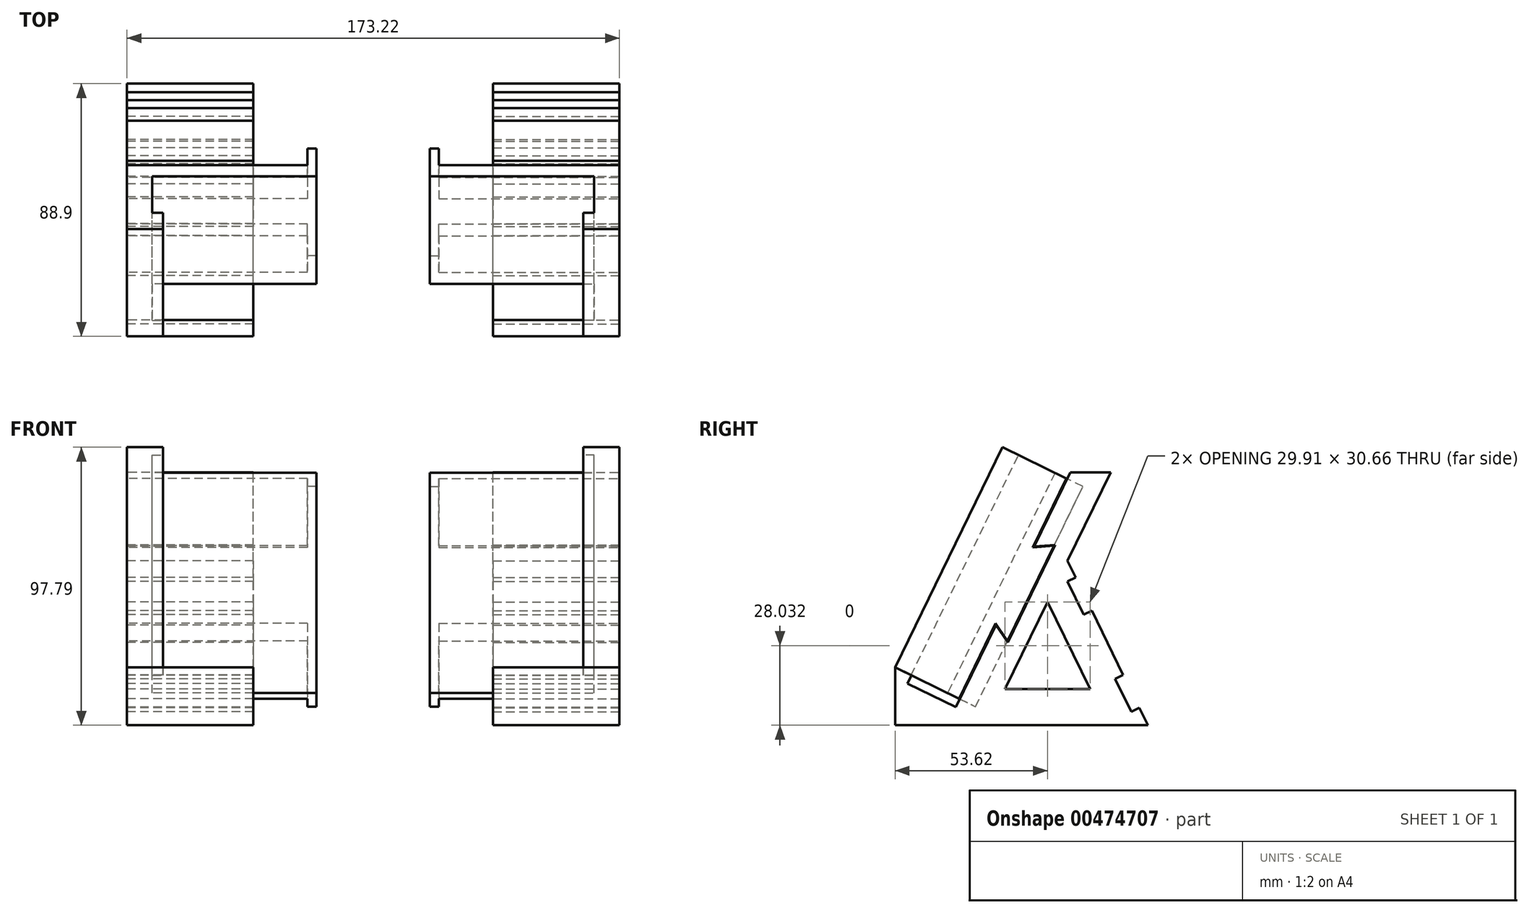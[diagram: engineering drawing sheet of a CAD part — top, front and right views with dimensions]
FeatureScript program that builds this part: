
annotation { "Feature Type Name" : "Feature", "Feature Type Description" : "" }
export const myFeature = defineFeature(function(context is Context, id is Id, definition is map)
    precondition{}
    {
        {
            var Q0;
            Q0=qCreatedBy(makeId("Front.planeOp"),FACE);
            var sketch = newSketch(context, id + "F0", { "sketchPlane" : qUnion([Q0])});
            skLineSegment(sketch, "E0.bottom", {"start": v(42.16, 0) * mm, "end": v(86.61, 0) * mm});
            skLineSegment(sketch, "E0.top", {"start": v(42.16, 88.9) * mm, "end": v(86.61, 88.9) * mm});
            skLineSegment(sketch, "E0.left", {"start": v(42.16, 0) * mm, "end": v(42.16, 88.9) * mm});
            skLineSegment(sketch, "E0.right", {"start": v(86.61, 0) * mm, "end": v(86.61, 88.9) * mm});
            skSolve(sketch);
        }
        {
            var Q0;
            Q0=makeQuery(id+"F0.imprint","IMPRINT",FACE,{"disambiguationData":[TD([[makeQuery(id+"F0.imprint","IMPRINT",EDGE,{"derivedFrom":sQuery(id+"F0.wireOp",EDGE,"E0.bottom")}),1.0]])]});
            extrude(context, id + "F1", {"entities" : qUnion([Q0]), "endBound" : BoundingType.SYMMETRIC, "depth" : 88.9 * mm});
        }
        {
            var Q0;
            Q0=makeQuery(id+"F1.opExtrude","SWEPT_FACE",FACE,{"disambiguationData":[OSD([sQuery(id+"F0.wireOp",EDGE,"E0.right")])]});
            var sketch = newSketch(context, id + "F2", { "sketchPlane" : qUnion([Q0])});
            skLineSegment(sketch, "E1", {"start": v(-44.45, 20.34) * mm, "end": v(-21.62, 9.2) * mm});
            skLineSegment(sketch, "E2", {"start": v(-21.62, 9.2) * mm, "end": v(17.25, 88.9) * mm});
            skLineSegment(sketch, "E3", {"start": v(-38.74, 17.55) * mm, "end": v(-40.13, 14.7) * mm});
            skLineSegment(sketch, "E4", {"start": v(-40.13, 14.7) * mm, "end": v(-23.01, 6.35) * mm});
            skLineSegment(sketch, "E5", {"start": v(-23.01, 6.35) * mm, "end": v(-21.62, 9.2) * mm});
            skLineSegment(sketch, "E6", {"start": v(17.25, 88.9) * mm, "end": v(-44.45, 88.9) * mm});
            skLineSegment(sketch, "E7", {"start": v(-44.45, 88.9) * mm, "end": v(-44.45, 20.34) * mm});
            skLineSegment(sketch, "E8", {"start": v(-8.93, 35.22) * mm, "end": v(-4.83, 29.15) * mm});
            skLineSegment(sketch, "E9", {"start": v(-4.83, 29.15) * mm, "end": v(11.87, 63.4) * mm});
            skLineSegment(sketch, "E10", {"start": v(11.87, 63.4) * mm, "end": v(4.56, 62.88) * mm});
            skLineSegment(sketch, "E11", {"start": v(-2.19, 49.05) * mm, "end": v(-44.45, 69.67) * mm});
            skLineSegment(sketch, "E12", {"start": v(-2.19, 49.05) * mm, "end": v(3.52, 46.27) * mm});
            skLineSegment(sketch, "E13", {"start": v(-5.79, 12.7) * mm, "end": v(24.13, 12.7) * mm});
            skLineSegment(sketch, "E14", {"start": v(24.13, 12.7) * mm, "end": v(9.17, 43.36) * mm});
            skLineSegment(sketch, "E15", {"start": v(9.17, 43.36) * mm, "end": v(-5.79, 12.7) * mm});
            skLineSegment(sketch, "E16", {"start": v(16.24, 57.85) * mm, "end": v(31.38, 88.9) * mm});
            skLineSegment(sketch, "E17", {"start": v(31.38, 88.9) * mm, "end": v(44.45, 88.9) * mm});
            skLineSegment(sketch, "E18", {"start": v(16.24, 57.85) * mm, "end": v(44.45, 0) * mm});
            skLineSegment(sketch, "E19", {"start": v(44.45, 0) * mm, "end": v(44.45, 88.9) * mm});
            skLineSegment(sketch, "E20", {"start": v(19.1, 51.98) * mm, "end": v(16.24, 50.6) * mm});
            skLineSegment(sketch, "E21", {"start": v(16.24, 50.6) * mm, "end": v(21.92, 38.95) * mm});
            skLineSegment(sketch, "E22", {"start": v(21.92, 38.95) * mm, "end": v(24.78, 40.34) * mm});
            skLineSegment(sketch, "E23", {"start": v(30.34, 28.92) * mm, "end": v(44.45, 35.8) * mm});
            skLineSegment(sketch, "E24.1.0.0", {"start": v(35.8, 17.74) * mm, "end": v(32.94, 16.35) * mm});
            skLineSegment(sketch, "E24.1.0.1", {"start": v(32.94, 16.35) * mm, "end": v(38.62, 4.7) * mm});
            skLineSegment(sketch, "E24.1.0.2", {"start": v(38.62, 4.7) * mm, "end": v(41.48, 6.1) * mm});
            skLineSegment(sketch, "E24.direction1", {"start": v(16.24, 50.6) * mm, "end": v(32.94, 16.35) * mm, "construction": true});
            skSolve(sketch);
        }
        {
            var Q0;
            Q0 = qSketchRegion(id + "F2", true);
            extrude(context, id + "F3", {"entities" : qUnion([Q0]), "operationType" : NewBodyOperationType.REMOVE, "endBound" : BoundingType.UP_TO_NEXT, "oppositeDirection" : true, "depth" : 25.4 * mm});
        }
        {
            var Q0;
            Q0=makeQuery(id+"F1.opExtrude","SWEPT_FACE",FACE,{"disambiguationData":[OSD([sQuery(id+"F0.wireOp",EDGE,"E0.right")])]});
            var sketch = newSketch(context, id + "F4", { "sketchPlane" : qUnion([Q0])});
            skLineSegment(sketch, "E25.0", {"start": v(11.45, 63.1) * mm, "end": v(4, 62.58) * mm});
            skLineSegment(sketch, "E25.1", {"start": v(-4.86, 29.65) * mm, "end": v(11.45, 63.1) * mm});
            skLineSegment(sketch, "E25.2", {"start": v(-9.05, 35.85) * mm, "end": v(-4.86, 29.65) * mm});
            skLineSegment(sketch, "E26", {"start": v(15.81, 86.82) * mm, "end": v(-21.96, 9.37) * mm});
            skLineSegment(sketch, "E27", {"start": v(15.81, 86.82) * mm, "end": v(-6.68, 97.79) * mm});
            skLineSegment(sketch, "E28", {"start": v(-6.68, 97.79) * mm, "end": v(-44.45, 20.34) * mm});
            skLineSegment(sketch, "E29", {"start": v(-44.45, 20.34) * mm, "end": v(-21.96, 9.37) * mm});
            skSolve(sketch);
        }
        {
            var Q0;
            Q0 = qSketchRegion(id + "F4", true);
            extrude(context, id + "F5", {"entities" : qUnion([Q0]), "oppositeDirection" : true, "depth" : 12.7 * mm});
        }
        {
            var Q0;
            Q0=makeQuery(id+"F5.opExtrude","CAP_FACE",FACE,{"disambiguationData":[OSD([sQuery(id+"F4.wireOp",EDGE,"E25.0"),sQuery(id+"F4.wireOp",EDGE,"E25.1"),sQuery(id+"F4.wireOp",EDGE,"E25.2"),sQuery(id+"F4.wireOp",EDGE,"E26"),sQuery(id+"F4.wireOp",EDGE,"E27"),sQuery(id+"F4.wireOp",EDGE,"E28"),sQuery(id+"F4.wireOp",EDGE,"E29")])],"isStart":false});
            var sketch = newSketch(context, id + "F6", { "sketchPlane" : qUnion([Q0])});
            skLineSegment(sketch, "E30.0", {"start": v(-15.81, 86.82) * mm, "end": v(-4, 62.58) * mm});
            skLineSegment(sketch, "E30.1", {"start": v(-11.45, 63.1) * mm, "end": v(-4, 62.58) * mm});
            skLineSegment(sketch, "E30.2", {"start": v(4.86, 29.65) * mm, "end": v(-11.45, 63.1) * mm});
            skLineSegment(sketch, "E30.3", {"start": v(9.05, 35.85) * mm, "end": v(4.86, 29.65) * mm});
            skLineSegment(sketch, "E30.4", {"start": v(9.05, 35.85) * mm, "end": v(21.96, 9.37) * mm});
            skLineSegment(sketch, "E31", {"start": v(-15.81, 86.82) * mm, "end": v(-11.82, 88.77) * mm});
            skLineSegment(sketch, "E32", {"start": v(-11.82, 88.77) * mm, "end": v(25.96, 11.32) * mm});
            skLineSegment(sketch, "E33", {"start": v(25.96, 11.32) * mm, "end": v(21.96, 9.37) * mm});
            skSolve(sketch);
        }
        {
            var Q0;
            Q0 = qSketchRegion(id + "F6", true);
            extrude(context, id + "F7", {"entities" : qUnion([Q0]), "operationType" : NewBodyOperationType.ADD, "depth" : 50.8 * mm});
        }
        {
            var Q0;
            Q0=makeQuery(id+"F7.opExtrude","CAP_FACE",FACE,{"disambiguationData":[OSD([sQuery(id+"F6.wireOp",EDGE,"E30.0"),sQuery(id+"F6.wireOp",EDGE,"E30.1"),sQuery(id+"F6.wireOp",EDGE,"E30.2"),sQuery(id+"F6.wireOp",EDGE,"E30.3"),sQuery(id+"F6.wireOp",EDGE,"E30.4"),sQuery(id+"F6.wireOp",EDGE,"E31"),sQuery(id+"F6.wireOp",EDGE,"E32"),sQuery(id+"F6.wireOp",EDGE,"E33")])],"isStart":false});
            var sketch = newSketch(context, id + "F8", { "sketchPlane" : qUnion([Q0])});
            skLineSegment(sketch, "E34", {"start": v(-11.82, 88.77) * mm, "end": v(25.96, 11.32) * mm});
            skLineSegment(sketch, "E35", {"start": v(25.96, 11.32) * mm, "end": v(16.14, 6.53) * mm});
            skLineSegment(sketch, "E36", {"start": v(16.14, 6.53) * mm, "end": v(-21.63, 83.98) * mm});
            skLineSegment(sketch, "E37", {"start": v(-21.63, 83.98) * mm, "end": v(-11.82, 88.77) * mm});
            skSolve(sketch);
        }
        {
            var Q0;
            Q0 = qSketchRegion(id + "F8", true);
            extrude(context, id + "F9", {"entities" : qUnion([Q0]), "operationType" : NewBodyOperationType.ADD, "depth" : 3.17 * mm});
        }
        {
            var Q0;
            Q0=makeQuery(id+"F9.boolean.opBoolean","MERGE",FACE,{"derivedFrom":[makeQuery(id+"F7.boolean.opBoolean","MERGE",FACE,{"derivedFrom":[makeQuery(id+"F5.opExtrude","SWEPT_FACE",FACE,{"disambiguationData":[OSD([sQuery(id+"F4.wireOp",EDGE,"E27")])]}),makeQuery(id+"F7.opExtrude","SWEPT_FACE",FACE,{"disambiguationData":[OSD([sQuery(id+"F6.wireOp",EDGE,"E31")])]})]}),makeQuery(id+"F9.opExtrude","SWEPT_FACE",FACE,{"disambiguationData":[OSD([sQuery(id+"F8.wireOp",EDGE,"E37")])]})]});
            var sketch = newSketch(context, id + "F10", { "sketchPlane" : qUnion([Q0])});
            skLineSegment(sketch, "E38", {"start": v(73.91, -28.3) * mm, "end": v(77.72, -28.3) * mm});
            skLineSegment(sketch, "E39", {"start": v(77.72, -28.3) * mm, "end": v(77.72, -42.58) * mm});
            skLineSegment(sketch, "E40", {"start": v(73.91, -42.58) * mm, "end": v(73.91, -28.3) * mm});
            skLineSegment(sketch, "E41", {"start": v(77.72, -42.58) * mm, "end": v(73.91, -42.58) * mm});
            skSolve(sketch);
        }
        {
            var Q0;
            Q0 = qSketchRegion(id + "F10", true);
            extrude(context, id + "F11", {"entities" : qUnion([Q0]), "operationType" : NewBodyOperationType.REMOVE, "endBound" : BoundingType.UP_TO_NEXT, "oppositeDirection" : true, "depth" : 25.4 * mm});
        }
        {
            var Q0;
            Q0=makeQuery(id+"F1.opExtrude","SWEPT_BODY",BODY,{"disambiguationData":[OSD([sQuery(id+"F0.wireOp",EDGE,"E0.bottom"),sQuery(id+"F0.wireOp",EDGE,"E0.top"),sQuery(id+"F0.wireOp",EDGE,"E0.left"),sQuery(id+"F0.wireOp",EDGE,"E0.right")])]});
            var Q1;
            Q1=makeQuery(id+"F5.opExtrude","SWEPT_BODY",BODY,{"disambiguationData":[OSD([sQuery(id+"F4.wireOp",EDGE,"E25.0"),sQuery(id+"F4.wireOp",EDGE,"E25.1"),sQuery(id+"F4.wireOp",EDGE,"E25.2"),sQuery(id+"F4.wireOp",EDGE,"E26"),sQuery(id+"F4.wireOp",EDGE,"E27"),sQuery(id+"F4.wireOp",EDGE,"E28"),sQuery(id+"F4.wireOp",EDGE,"E29")])]});
            var Q2;
            Q2=qCreatedBy(makeId("Right.planeOp"),FACE);
            mirror(context, id + "F12", {"entities" : qUnion([Q0, Q1]), "mirrorPlane" : qUnion([Q2])});
        }
    });
